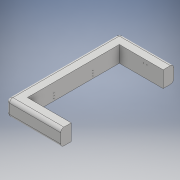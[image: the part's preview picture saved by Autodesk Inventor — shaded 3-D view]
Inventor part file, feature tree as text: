
AUTODESK INVENTOR PART (.ipt)
format: ipt  version: 2018 (Build 220112000, 112)  size: 170,496 bytes
history: native  units: in
note: dims shown in document units (in); Inventor stores cm internally (conversion verified against a paired STEP export)
features: extrude x4, sketch x4, fillet x1
ambient origin geometry x8: Origin, YZ Plane, XZ Plane, XY Plane, X Axis, Y Axis, Z Axis, Center Point
bodies: Solid1 (feature_tree)
feature tree (9):
  extrude  "Extrusion1"  Depth=13.5in
  fillet  "Fillet1"  Radius=3.25in
  sketch  "Sketch2"  dims[d3=5.0in d4=0.0in d5=1.0in]
  extrude  "Extrusion3"  Depth=1.0in
  extrude  "Extrusion4"  Depth=4.0in
  extrude  "Extrusion5"  Depth=1.0in
  sketch  "Sketch1"  dims[d0=28.31in d1=13.5in d2=3.25in]
  sketch  "Sketch3"  dims[d15=0.375in d16=4.0in]
  sketch  "Sketch4"  dims[d17=1.75in d18=1.75in d19=1.0in d20=0.21in d21=0.1875in d22=0.0in d23=8.155in d24=2.83in d25=0.75in d26=0.75in d27=0.21in d28=0.1875in d29=0.0in d30=7.5in d31=3.83in d32=90.0deg d33=1.0in d34=0.2031in d35=1.0in d36=0.0in]
